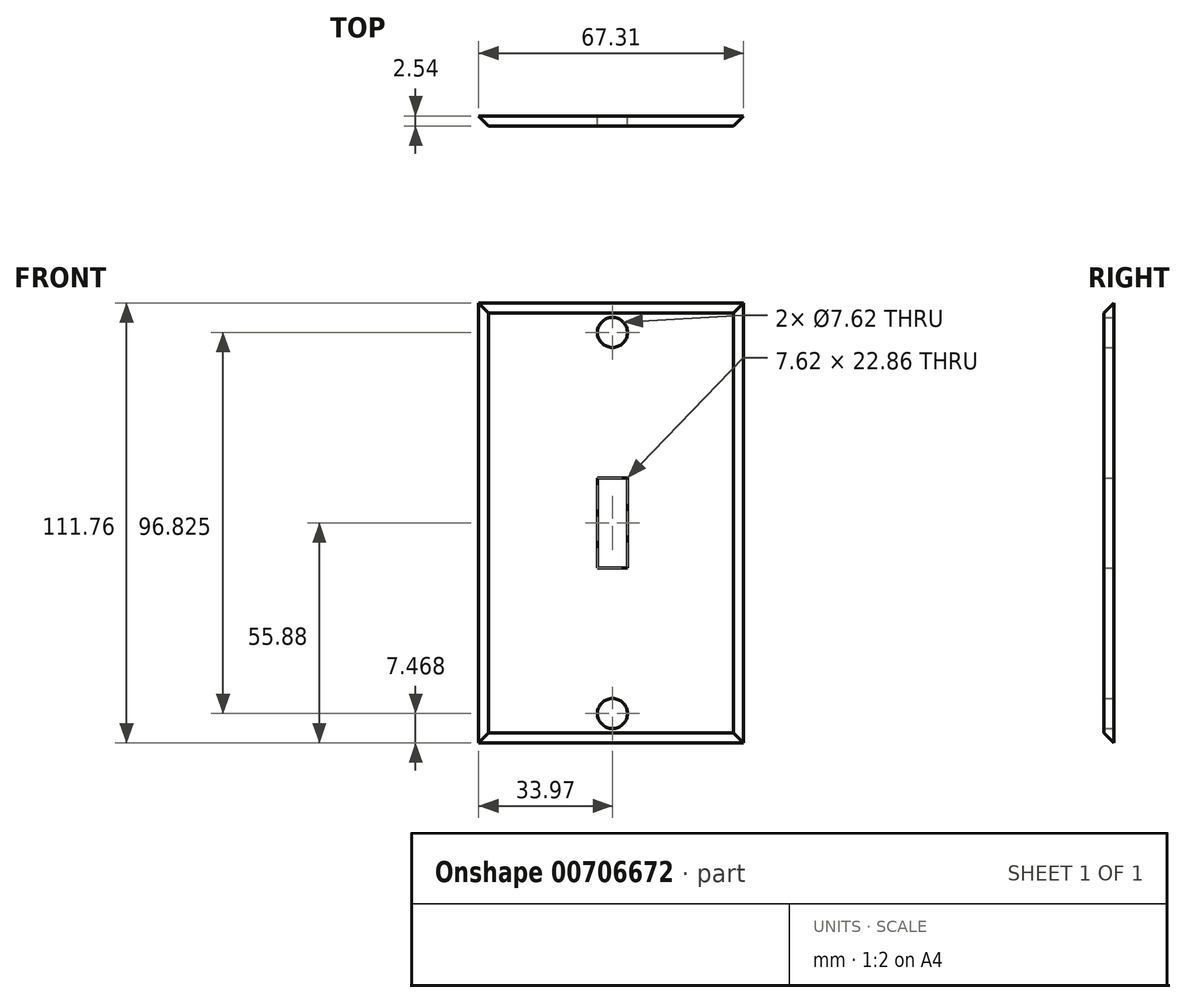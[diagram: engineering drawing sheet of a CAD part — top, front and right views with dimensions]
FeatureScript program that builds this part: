
annotation { "Feature Type Name" : "Feature", "Feature Type Description" : "" }
export const myFeature = defineFeature(function(context is Context, id is Id, definition is map)
    precondition{}
    {
        {
            var Q0;
            Q0=qCreatedBy(makeId("Front.planeOp"),FACE);
            var sketch = newSketch(context, id + "F0", { "sketchPlane" : qUnion([Q0])});
            skLineSegment(sketch, "E0.bottom", {"start": v(-35.24, 57.15) * mm, "end": v(34.61, 57.15) * mm});
            skLineSegment(sketch, "E0.top", {"start": v(-35.24, -57.15) * mm, "end": v(34.61, -57.15) * mm});
            skLineSegment(sketch, "E0.left", {"start": v(-35.24, 57.15) * mm, "end": v(-35.24, -57.15) * mm});
            skLineSegment(sketch, "E0.right", {"start": v(34.61, 57.15) * mm, "end": v(34.61, -57.15) * mm});
            skCircle(sketch, "E1", {"center": v(0, -48.41) * mm, "radius": 3.81 * mm});
            skCircle(sketch, "E2", {"center": v(0, 48.41) * mm, "radius": 3.81 * mm});
            skPoint(sketch, "E3.start.orphan", {"position": v(-35.24, 0) * mm});
            skLineSegment(sketch, "E4", {"start": v(0, 11.43) * mm, "end": v(-3.8, 11.43) * mm});
            skLineSegment(sketch, "E5", {"start": v(0, 11.43) * mm, "end": v(3.81, 11.43) * mm});
            skLineSegment(sketch, "E6", {"start": v(-3.8, 11.43) * mm, "end": v(-3.8, -11.43) * mm});
            skLineSegment(sketch, "E7", {"start": v(-3.8, -11.43) * mm, "end": v(3.81, -11.43) * mm});
            skLineSegment(sketch, "E8", {"start": v(3.81, -11.43) * mm, "end": v(3.81, 11.43) * mm});
            skPoint(sketch, "E9.start.orphan", {"position": v(-10.8, 11.43) * mm});
            skPoint(sketch, "E10.start.orphan", {"position": v(22.48, -55.37) * mm});
            skPoint(sketch, "E11.end.orphan", {"position": v(5.84, -55.37) * mm});
            skPoint(sketch, "E11.start.orphan", {"position": v(-10.8, -55.37) * mm});
            skPoint(sketch, "E12.start.orphan", {"position": v(-32.7, 0) * mm});
            skPoint(sketch, "E13.orphan", {"position": v(-26.06, 0) * mm});
            skPoint(sketch, "E14.end.orphan", {"position": v(-20.6, 30.84) * mm});
            skPoint(sketch, "E15.end.orphan", {"position": v(-26.65, 15.42) * mm});
            skSolve(sketch);
        }
        {
            var Q0;
            Q0=makeQuery(id+"F0.imprint","IMPRINT",FACE,{"disambiguationData":[TD([[makeQuery(id+"F0.imprint","IMPRINT",EDGE,{"derivedFrom":sQuery(id+"F0.wireOp",EDGE,"E0.bottom")}),-1.0]])]});
            extrude(context, id + "F1", {"entities" : qUnion([Q0]), "depth" : 2.54 * mm, "offsetDistance" : 25.4 * mm});
        }
        {
            var Q0;
            Q0=makeQuery(id+"F1.opExtrude","CAP_EDGE",EDGE,{"disambiguationData":[OSD([sQuery(id+"F0.wireOp",EDGE,"E0.bottom")])],"isStart":false});
            var Q1;
            Q1=makeQuery(id+"F1.opExtrude","CAP_EDGE",EDGE,{"disambiguationData":[OSD([sQuery(id+"F0.wireOp",EDGE,"E0.left")])],"isStart":false});
            var Q2;
            Q2=makeQuery(id+"F1.opExtrude","CAP_EDGE",EDGE,{"disambiguationData":[OSD([sQuery(id+"F0.wireOp",EDGE,"E0.right")])],"isStart":false});
            var Q3;
            Q3=makeQuery(id+"F1.opExtrude","CAP_EDGE",EDGE,{"disambiguationData":[OSD([sQuery(id+"F0.wireOp",EDGE,"E0.top")])],"isStart":false});
            chamfer(context, id + "F2", {"entities" : qUnion([Q0, Q1, Q2, Q3]), "width" : 3.8 * mm, "tangentPropagation" : true});
        }
    });
